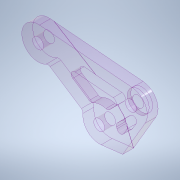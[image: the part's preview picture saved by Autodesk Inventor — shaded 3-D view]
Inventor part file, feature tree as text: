
AUTODESK INVENTOR PART (.ipt)
format: ipt  version: 2020.2 (Build 242310000, 310)  size: 574,976 bytes
history: native  units: mm
features: extrude x20, sketch x11, projected_geometry x11, other x3, fillet x3, hole x2
ambient origin geometry x8: Origin, YZ Plane, XZ Plane, XY Plane, X Axis, Y Axis, Z Axis, Center Point
bodies: Body1 (feature_tree)
feature tree (50):
  other  "ソリッド1"
  sketch  "スケッチ1"
  extrude  "押し出し1"  Depth=3.0mm TaperAngle=0.0deg
  extrude  "押し出し2"  Depth=0.05mm TaperAngle=0.0deg
  extrude  "押し出し3"  Depth=6.0mm
  sketch  "スケッチ3"
  extrude  "押し出し4"  Depth=1.0mm TaperAngle=0.0deg
  extrude  "押し出し5"  Depth=10.0mm TaperAngle=0.0deg
  hole  "穴1"  [1 undecoded]
  sketch  "スケッチ4"
  extrude  "押し出し6"  Depth=9.0mm
  extrude  "押し出し7"  Depth=9.0mm
  extrude  "押し出し8"  Depth=10.0mm TaperAngle=0.0deg
  extrude  "押し出し9"  Depth=3.0mm TaperAngle=0.0deg
  sketch  "スケッチ5"
  extrude  "押し出し10"  Depth=0.05mm TaperAngle=0.0deg
  extrude  "押し出し12"  Depth=0.05mm TaperAngle=0.0deg
  extrude  "押し出し13"  Depth=3.0mm TaperAngle=0.0deg
  extrude  "押し出し14"  Depth=0.05mm TaperAngle=0.0deg
  extrude  "押し出し11"  Depth=9.0mm
  hole  "穴2"  [1 undecoded]
  sketch  "スケッチ6"
  extrude  "押し出し15"  Depth=3.0mm TaperAngle=0.0deg
  extrude  "押し出し16"  Depth=10.0mm TaperAngle=0.0deg
  extrude  "押し出し17"  Depth=3.0mm TaperAngle=0.0deg
  extrude  "押し出し18"  Depth=0.05mm TaperAngle=0.0deg
  fillet  "フィレット1"  Radius=1.0mm
  extrude  "押し出し19"  Depth=1.0mm TaperAngle=0.0deg
  fillet  "フィレット2"  Radius=3.0mm
  extrude  "押し出し20"  Depth=1.0mm
  fillet  "フィレット3"  Radius=3.0mm
  sketch  "スケッチ11"
  sketch  "スケッチ2"
  projected_geometry  "投影ループ1"
  projected_geometry  "投影ループ2"
  projected_geometry  "投影ループ3"
  projected_geometry  "投影ループ4"
  projected_geometry  "投影ループ5"
  sketch  "スケッチ7"
  projected_geometry  "投影ループ6"
  sketch  "スケッチ8"
  sketch  "スケッチ9"
  projected_geometry  "投影ループ7"
  sketch  "スケッチ10"
  projected_geometry  "投影ループ8"
  projected_geometry  "投影ループ9"
  projected_geometry  "投影ループ10"
  projected_geometry  "投影ループ11"
  other  "断面エッジを投影1"
  other  "断面エッジを投影2"
note: 2 required parameter values undecoded (feature->parameter linkage not recoverable at this tier; creation-order binding heuristic only, values carry confidence <= 0.55)
